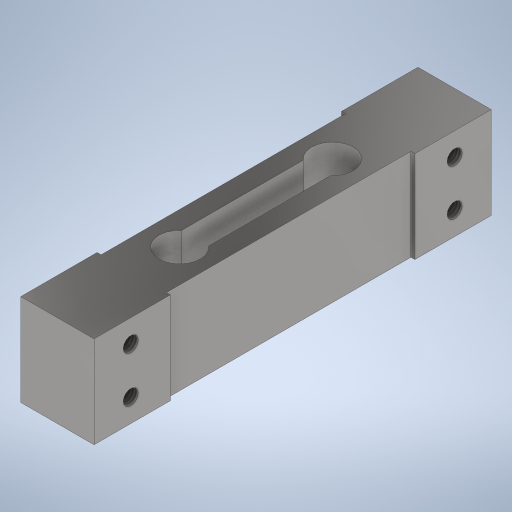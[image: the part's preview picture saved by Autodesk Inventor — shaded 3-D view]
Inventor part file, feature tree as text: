
AUTODESK INVENTOR PART (.ipt)
format: ipt  version: 2023 (Build 270158000, 158)  size: 306,176 bytes
history: native  units: mm
features: sketch x2, other x1, extrude x1, hole x1
ambient origin geometry x8: Origin, YZ Plane, XZ Plane, XY Plane, X Axis, Y Axis, Z Axis, Center Point
bodies: Body1 (feature_tree)
feature tree (5):
  other  "Sólido1"
  extrude  "Extrusão1"  Depth=130.0mm
  hole  "Furo1"  [1 undecoded]
  sketch  "Esboço1"  dims[d0=24.0mm d1=130.0mm]
  sketch  "Esboço2"  dims[d2=13.5mm d3=12.0mm d4=12.0mm d8=0.0mm d9=1.3mm d10=80.0mm d11=1.3mm d12=80.0mm d13=0.0mm d14=0.0mm d15=0.0mm d16=0.0mm d17=30.0mm d18=0.0mm d19=12.0mm d20=12.0mm d21=12.0mm d22=12.0mm d23=7.5mm d24=7.5mm d25=7.5mm d26=7.5mm d27=4.917mm d28=40.0mm d29=4.0mm d30=2.0mm d31=90.0deg d32=17.1mm d33=20.594885mm d34=8.8mm d37=0.0mm d38=4.4mm d39=50.0mm d40=25.0mm d41=25.0mm d35=1.0mm d36=1.0mm d42=20.594885mm d43=0.0625mm d44=0.75mm d45=0.375mm]
note: 1 required parameter value undecoded (feature->parameter linkage not recoverable at this tier; creation-order binding heuristic only, values carry confidence <= 0.55)
